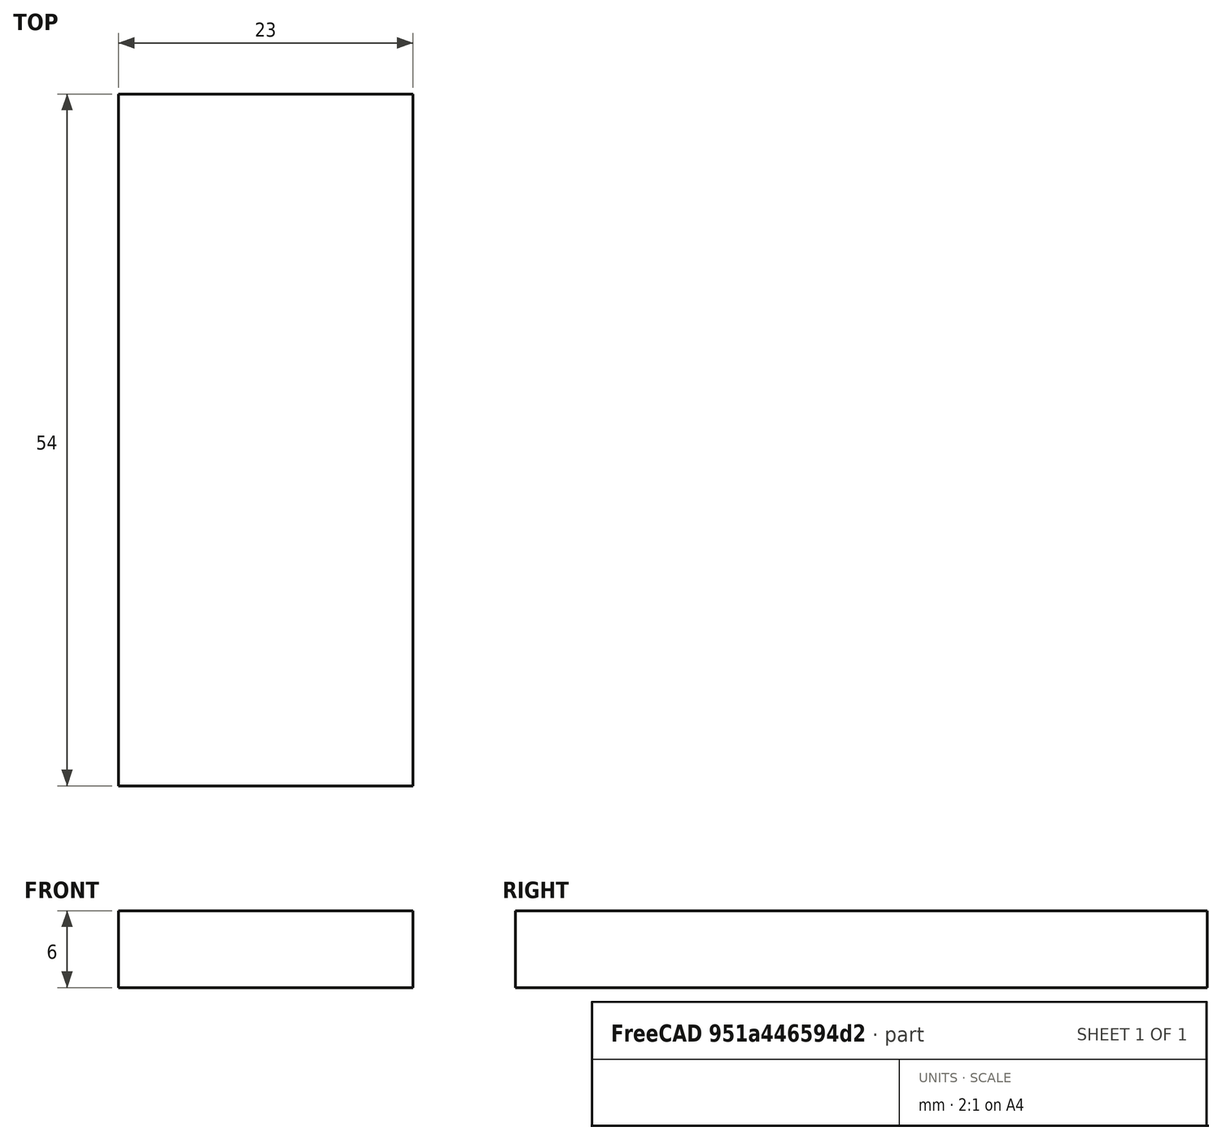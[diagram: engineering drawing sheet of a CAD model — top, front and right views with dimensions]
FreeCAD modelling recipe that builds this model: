
FCSTD DOCUMENT  (FreeCAD 0.17R13541 (Git))
Label: TechNicolor-Triangle-39-battery-D1-Mini-USB-BMS-Big-Filleted-Channel-And-USB-alt-Solid-Back-through
License: All rights reserved
LicenseURL: http://en.wikipedia.org/wiki/All_rights_reserved
objects: Part::Cut×8, Part::Box×6, Part::Prism×4, Part::Fillet×2
note: 20 computed .brp shape members not serialized (recipe doc carries the construction recipe); baked Part::Feature solids carry a one-line shape summary decoded from their .brp

FEATURE [Part::Prism] Prism
  AttacherType = Attacher::AttachEngine3D
  Circumradius = 165
  Height = 25
  Placement = pos=(0,0,-6) rot=(0,0,1;0rad)
  Polygon = 3
FEATURE [Part::Prism] Prism001
  AttacherType = Attacher::AttachEngine3D
  Circumradius = 95
  Height = 25
  Placement = pos=(0,0,-6) rot=(0,0,1;0rad)
  Polygon = 3
FEATURE [Part::Cut] Cut
  Base = -> Prism
  Tool = -> Prism001
FEATURE [Part::Box] Box
  AttacherType = Attacher::AttachEngine3D
  Height = 19
  Length = 70
  Placement = pos=(-2,65,0) rot=(0,0,-1;0.523599rad)
  Width = 19
FEATURE [Part::Cut] Cut001
  Base = -> Cut
  Tool = -> Box
FEATURE [Part::Box] Box001
  AttacherType = Attacher::AttachEngine3D
  Height = 19
  Length = 70
  Placement = pos=(-55,-35,0) rot=(0,0,1;1.5708rad)
  Width = 19
FEATURE [Part::Cut] Cut002
  Base = -> Cut001
  Tool = -> Box001
FEATURE [Part::Box] Box002
  AttacherType = Attacher::AttachEngine3D
  Height = 19
  Length = 70
  Placement = pos=(7,-82,0) rot=(0,0,1;0.523599rad)
  Width = 19
FEATURE [Part::Cut] Cut003
  Base = -> Cut002
  Tool = -> Box002
FEATURE [Part::Box] Box003
  AttacherType = Attacher::AttachEngine3D
  Height = 10
  Length = 35
  Placement = pos=(93,-13.3,9) rot=(0,0,1;0rad)
  Width = 26.5
FEATURE [Part::Cut] Cut004
  Base = -> Cut003
  Tool = -> Box003
FEATURE [Part::Box] Box004
  AttacherType = Attacher::AttachEngine3D
  Height = 4
  Length = 10
  Placement = pos=(84,-6,15) rot=(0,0,1;0rad)
  Width = 12
FEATURE [Part::Cut] Cut005
  Base = -> Cut004
  Tool = -> Box004
FEATURE [Part::Box] Box005
  AttacherType = Attacher::AttachEngine3D
  Height = 6
  Length = 23
  Placement = pos=(-76,34,13) rot=(0,0,1;0rad)
  Width = 54
FEATURE [Part::Prism] Prism002
  AttacherType = Attacher::AttachEngine3D
  Circumradius = 152
  Height = 6
  Placement = pos=(0,0,13) rot=(0,0,1;0rad)
  Polygon = 3
FEATURE [Part::Prism] Prism003
  AttacherType = Attacher::AttachEngine3D
  Circumradius = 106
  Height = 6
  Placement = pos=(0,0,13) rot=(0,0,1;0rad)
  Polygon = 3
FEATURE [Part::Cut] Cut006
  Base = -> Prism002
  Tool = -> Prism003
FEATURE [Part::Cut] Cut007
  Base = -> Cut005
  Tool = -> Cut006
FEATURE [Part::Fillet] Fillet
  Base = -> Cut007
  Edges = 4 edges r=0.8: [Edge86,Edge89,Edge98,Edge100]
FEATURE [Part::Fillet] Fillet001
  Base = -> Fillet
  Edges = 2 edges r=4: [Edge101,Edge110]
